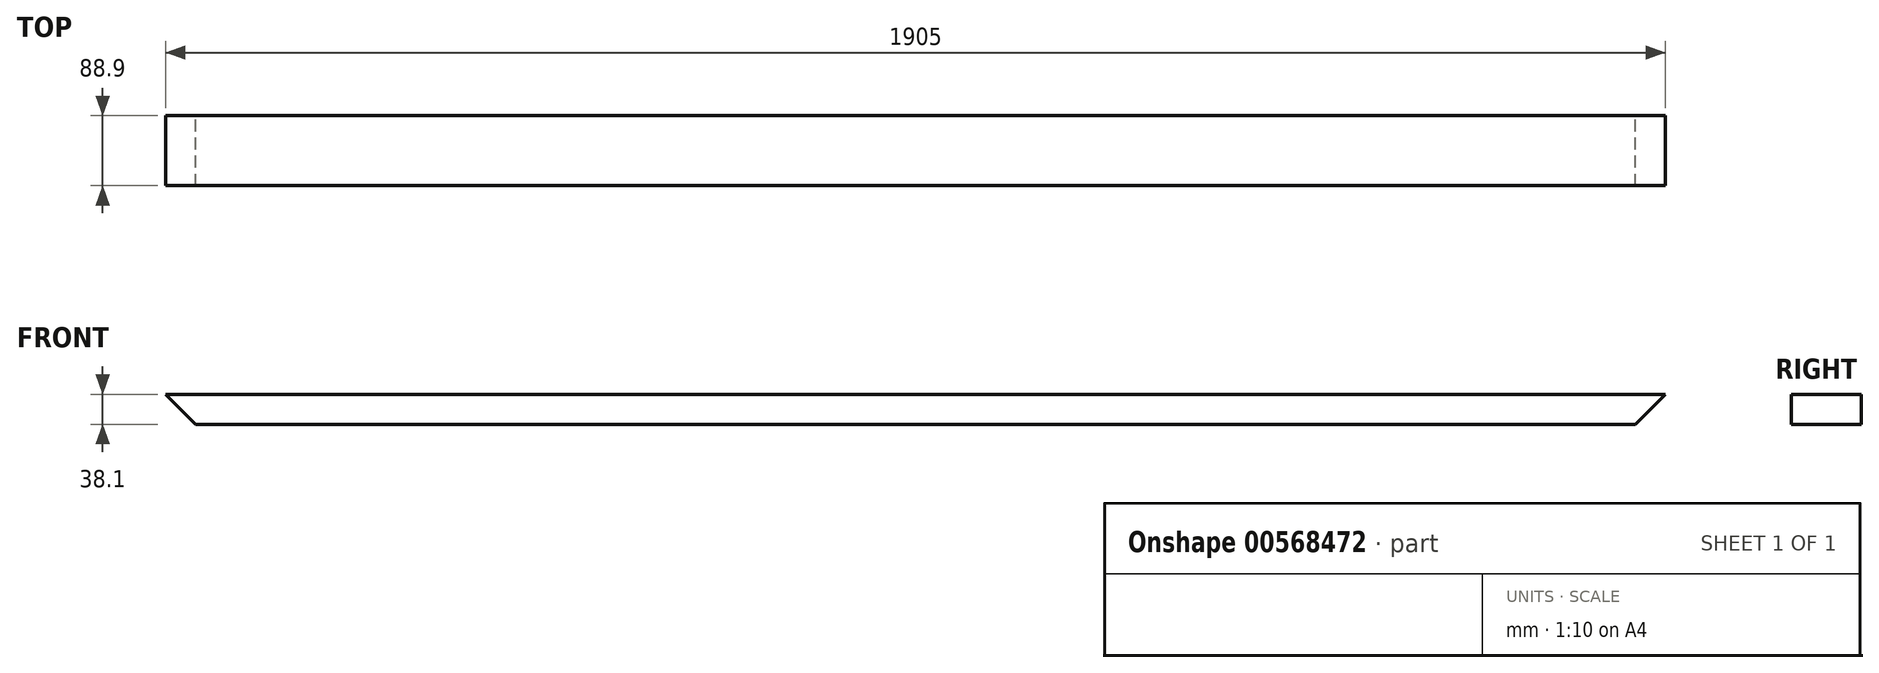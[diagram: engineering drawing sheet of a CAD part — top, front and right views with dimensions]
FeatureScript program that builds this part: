
annotation { "Feature Type Name" : "Feature", "Feature Type Description" : "" }
export const myFeature = defineFeature(function(context is Context, id is Id, definition is map)
    precondition{}
    {
        {
            var Q0;
            Q0=qCreatedBy(makeId("Front.planeOp"),FACE);
            var sketch = newSketch(context, id + "F0", { "sketchPlane" : qUnion([Q0])});
            skLineSegment(sketch, "E0", {"start": v(0, 0) * mm, "end": v(125.56, 0) * mm});
            skLineSegment(sketch, "E1", {"start": v(125.56, 0) * mm, "end": v(163.66, 38.1) * mm});
            skLineSegment(sketch, "E2", {"start": v(163.66, 38.1) * mm, "end": v(-1741.34, 38.1) * mm});
            skLineSegment(sketch, "E3", {"start": v(-1741.34, 38.1) * mm, "end": v(-1703.24, 0) * mm});
            skLineSegment(sketch, "E4", {"start": v(-1703.24, 0) * mm, "end": v(0, 0) * mm});
            skSolve(sketch);
        }
        {
            var Q0;
            Q0 = qSketchRegion(id + "F0", true);
            extrude(context, id + "F1", {"entities" : qUnion([Q0]), "depth" : 88.9 * mm, "offsetDistance" : 25.4 * mm});
        }
    });
